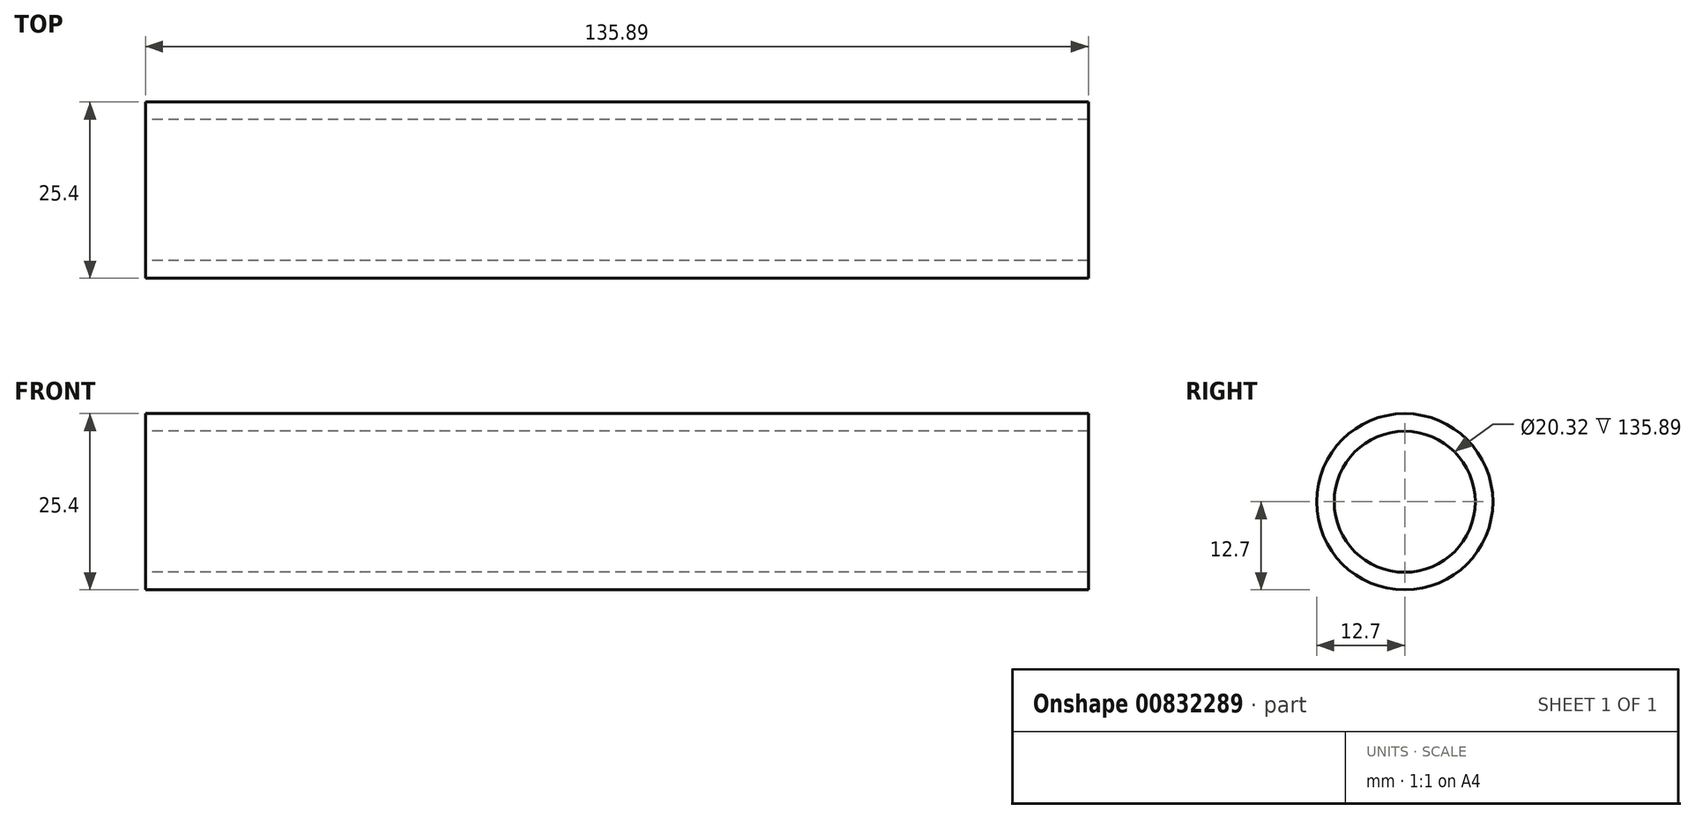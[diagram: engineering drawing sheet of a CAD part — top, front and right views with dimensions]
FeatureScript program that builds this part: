
annotation { "Feature Type Name" : "Feature", "Feature Type Description" : "" }
export const myFeature = defineFeature(function(context is Context, id is Id, definition is map)
    precondition{}
    {
        {
            var Q0;
            Q0=qCreatedBy(makeId("Right.planeOp"),FACE);
            var sketch = newSketch(context, id + "F0", { "sketchPlane" : qUnion([Q0])});
            skCircle(sketch, "E0", {"center": v(0, 0) * mm, "radius": 12.7 * mm});
            skSolve(sketch);
        }
        {
            var Q0;
            Q0=makeQuery(id+"F0.imprint","IMPRINT",FACE,{"disambiguationData":[TD([[makeQuery(id+"F0.imprint","IMPRINT",EDGE,{"derivedFrom":sQuery(id+"F0.wireOp",EDGE,"E0")}),1.0]])]});
            extrude(context, id + "F1", {"entities" : qUnion([Q0]), "depth" : 135.89 * mm, "offsetDistance" : 25.4 * mm});
        }
        {
            var Q0;
            Q0=makeQuery(id+"F1.opExtrude","CAP_FACE",FACE,{"disambiguationData":[OSD([sQuery(id+"F0.wireOp",EDGE,"E0")])],"isStart":false});
            var Q1;
            Q1=makeQuery(id+"F1.opExtrude","CAP_FACE",FACE,{"disambiguationData":[OSD([sQuery(id+"F0.wireOp",EDGE,"E0")])],"isStart":true});
            shell(context, id + "F2", {"entities" : qUnion([Q0, Q1]), "thickness" : 2.54 * mm});
        }
    });
